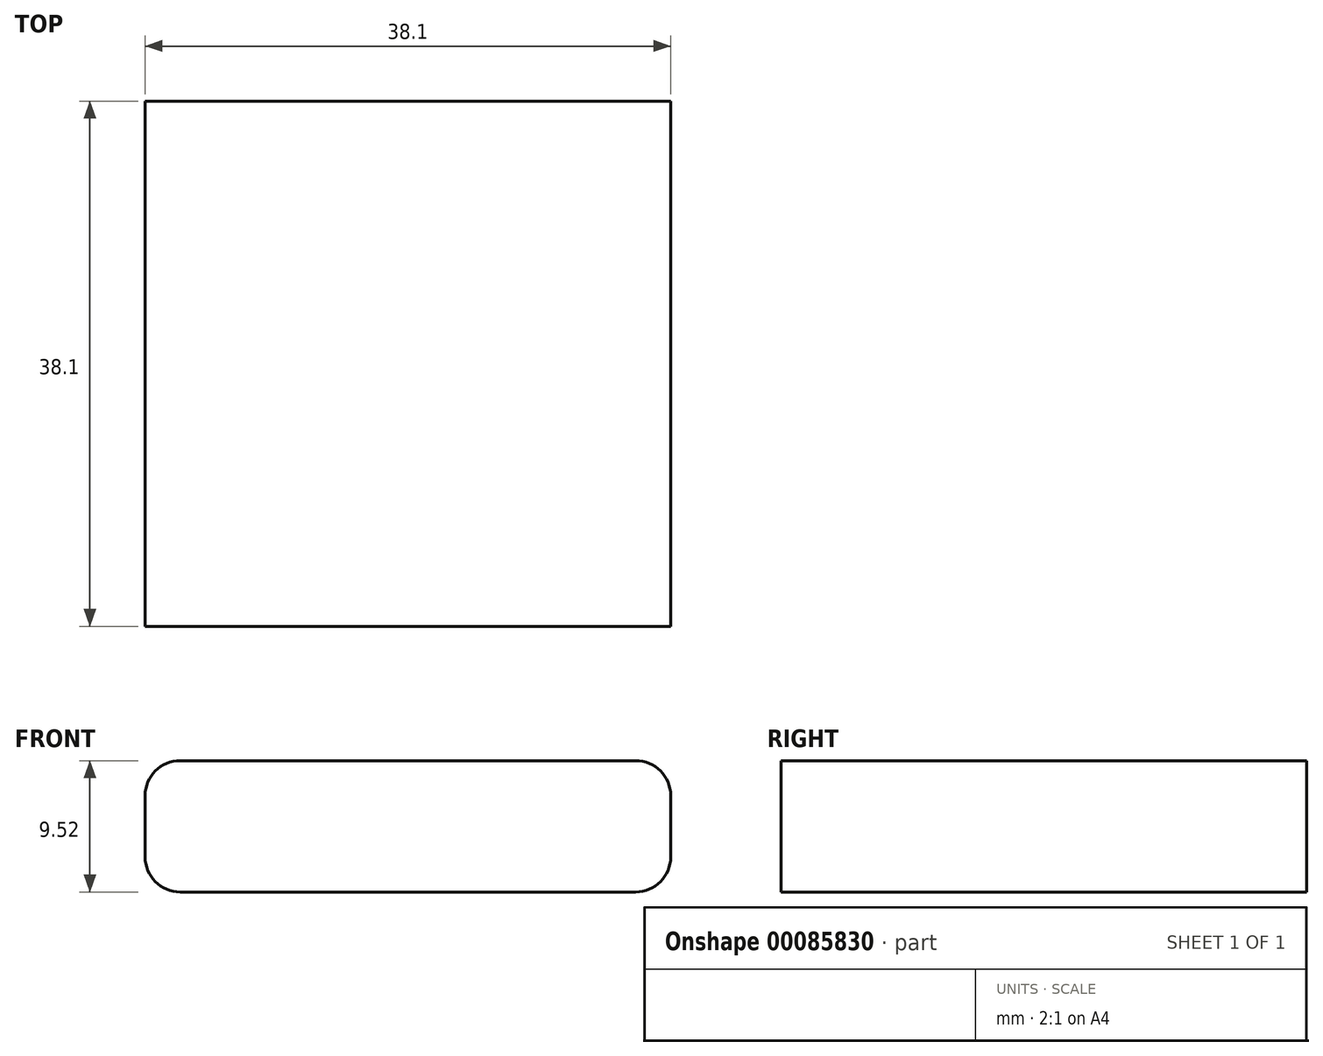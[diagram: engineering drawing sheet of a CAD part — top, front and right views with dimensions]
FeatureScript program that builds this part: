
annotation { "Feature Type Name" : "Feature", "Feature Type Description" : "" }
export const myFeature = defineFeature(function(context is Context, id is Id, definition is map)
    precondition{}
    {
        {
            var Q0;
            Q0=qCreatedBy(makeId("Front.planeOp"),FACE);
            var sketch = newSketch(context, id + "F0", { "sketchPlane" : qUnion([Q0])});
            skLineSegment(sketch, "E0.bottom", {"start": v(-15.36, 20.48) * mm, "end": v(-53.46, 20.48) * mm});
            skLineSegment(sketch, "E0.top", {"start": v(-15.36, 30) * mm, "end": v(-53.46, 30) * mm});
            skLineSegment(sketch, "E0.left", {"start": v(-15.36, 20.48) * mm, "end": v(-15.36, 30) * mm});
            skLineSegment(sketch, "E0.right", {"start": v(-53.46, 20.48) * mm, "end": v(-53.46, 30) * mm});
            skSolve(sketch);
        }
        {
            var Q0;
            Q0=makeQuery(id+"F0.imprint","IMPRINT",FACE,{"disambiguationData":[TD([[makeQuery(id+"F0.imprint","IMPRINT",EDGE,{"derivedFrom":sQuery(id+"F0.wireOp",EDGE,"E0.bottom")}),-1.0]])]});
            extrude(context, id + "F1", {"entities" : qUnion([Q0]), "depth" : 38.1 * mm, "offsetDistance" : 25.4 * mm});
        }
        {
            var Q0;
            Q0=makeQuery(id+"F1.opExtrude","SWEPT_EDGE",EDGE,{"disambiguationData":[OSD([sQuery(id+"F0.wireOp",EDGE,"E0.top"),sQuery(id+"F0.wireOp",EDGE,"E0.left")])]});
            var Q1;
            Q1=makeQuery(id+"F1.opExtrude","SWEPT_EDGE",EDGE,{"disambiguationData":[OSD([sQuery(id+"F0.wireOp",EDGE,"E0.top"),sQuery(id+"F0.wireOp",EDGE,"E0.right")])]});
            var Q2;
            Q2=makeQuery(id+"F1.opExtrude","SWEPT_EDGE",EDGE,{"disambiguationData":[OSD([sQuery(id+"F0.wireOp",EDGE,"E0.bottom"),sQuery(id+"F0.wireOp",EDGE,"E0.right")])]});
            var Q3;
            Q3=makeQuery(id+"F1.opExtrude","SWEPT_EDGE",EDGE,{"disambiguationData":[OSD([sQuery(id+"F0.wireOp",EDGE,"E0.bottom"),sQuery(id+"F0.wireOp",EDGE,"E0.left")])]});
            fillet(context, id + "F2", {"entities" : qUnion([Q0, Q1, Q2, Q3]), "radius" : 2.54 * mm, "tangentPropagation" : true, "allowEdgeOverflow" : false});
        }
    });
